# Revit family: Faucet-Two_Handle-American_Standard-Metering-134022X_Series
name_source: partatom
category: Plumbing Fixtures
units: mm (PartAtom-declared; Revit-internal decimal feet)

## family parameters
Always vertical = No
Cut with Voids When Loaded = No
OmniClass Number = 23.45.55.17
OmniClass Title = Mixing Faucets
Part Type = Normal
Room Calculation Point = No
Round Connector Dimension = Use Diameter
Shared = Yes
Work Plane-Based = Yes

## types (2) — shared parameters
ADA Compliant = Yes
Assembly Code = D2020300
CEC Compliant = Yes
CW Connection = Yes
CWFU = 1.5
CalGreen Compliant = Yes
Cold Water Connection Diameter = 1/2"
Compliance Certifications = These products meet or exceed the following codes and standards: ANSI A117.1, ASME A112.18.1, CSA B 125
NSF 61/Section 9 and Annex G, CALGreen
Default Elevation = 0"
Description = Metering 4-Inch Centerset 2-Handle Faucet 0.5 gpm/1.9 Lpf
Finish = Brass-American Standard-002-Polished Chrome
HW Connection = Yes
HWFU = 1.5
Height = 3 3/8"
Hot Water Connection Diameter = 1/2"
Installation Type = Deck Mounted
Length = 4 5/8"
Manufacturer = American Standard
Material = Brass-American Standard-002-Polished Chrome
Minimum Operating Pressure = 20 psi
Product Documentation Link = https://americanstandard.box.com
Product Page URL = https://www.americanstandard-us.com
URL = https://www.americanstandard-us.com
Vent Connection = No
WFU = 2
Waste Connection = No
Width = 6"

## per-type parameters (varying)
| type | Flow Rate |
| 1340227.002 | 0.5 gpm (1.9 Lpf) |
| 1340225.002 | 1.0 gpm (3.8 Lpf) |

note: column(s) folded — value = type name in every type: Model

## geometry (parser evidence)
native form markers: Sweep x3
no freeform markers — native parametric forms only
